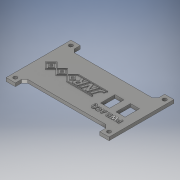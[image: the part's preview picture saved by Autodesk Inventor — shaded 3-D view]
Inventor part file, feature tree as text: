
AUTODESK INVENTOR PART (.ipt)
format: ipt  version: 2018 (Build 220112000, 112)  size: 1,207,296 bytes
history: native  units: in
note: dims shown in document units (in); Inventor stores cm internally (conversion verified against a paired STEP export)
features: sketch x6, extrude x4, move_body x3, emboss x2, direct_edit x2, chamfer x1
ambient origin geometry x8: Origin, YZ Plane, XZ Plane, XY Plane, X Axis, Y Axis, Z Axis, Center Point
bodies: Solid1 (feature_tree)
feature tree (18):
  extrude  "Extrusion1"  Depth=0.36in
  extrude  "Extrusion2"  Depth=0.36in
  extrude  "Extrusion3"  Depth=0.36in
  emboss  "Emboss1"
  emboss  "Emboss2"
  extrude  "Extrusion4"  Depth=0.125in TaperAngle=0.0deg
  chamfer  "Chamfer1"  Distance=0.146in
  direct_edit  "Direct Edit1"
  direct_edit  "Direct Edit2"
  sketch  "Sketch1"  dims[d0=2.311in d1=0.36in]
  sketch  "Sketch2"  dims[d2=0.36in d3=0.36in]
  sketch  "Sketch3"  dims[d4=0.36in d5=0.36in]
  sketch  "Sketch5"  dims[d7=0.36in d8=0.125in d9=0.0in]
  sketch  "Sketch6"  dims[d10=0.146in]
  sketch  "Sketch7"  dims[d11=0.146in d12=0.146in d13=0.146in d14=1.0in d15=0.0in d16=3.9in d17=0.18in d18=0.181in d19=0.18in d20=0.18in d21=0.181in d22=0.18in d23=0.18in d24=0.18in d25=0.56in d26=0.35in d27=0.35in d28=0.25in d30=1.0in d31=0.0in d32=0.36in d34=270.0deg d35=270.0deg d37=0.02in d38=0.0in d39=0.033in d40=0.025in d41=0.1in d42=1.2in d43=0.025in d44=0.0325in d45=45.0deg d46=0.4in d47=0.2in d48=0.175in d49=0.175in d50=1.0625in d51=0.045in d52=0.0329in d53=0.045in d54=0.0325in d55=0.045in d56=0.0in d59=270.0deg d60=0.03in d61=0.0in d62=1.0in d63=0.0in d64=0.125in d65=0.125in d66=45.0deg d67=0.0in d68=0.0in d69=0.105in d70=0.0in d71=0.0in d72=0.105in d73=-0.1in d74=0.0in d75=0.0in]
  move_body  "Move1"
  move_body  "Move2"
  move_body  "Move3"
